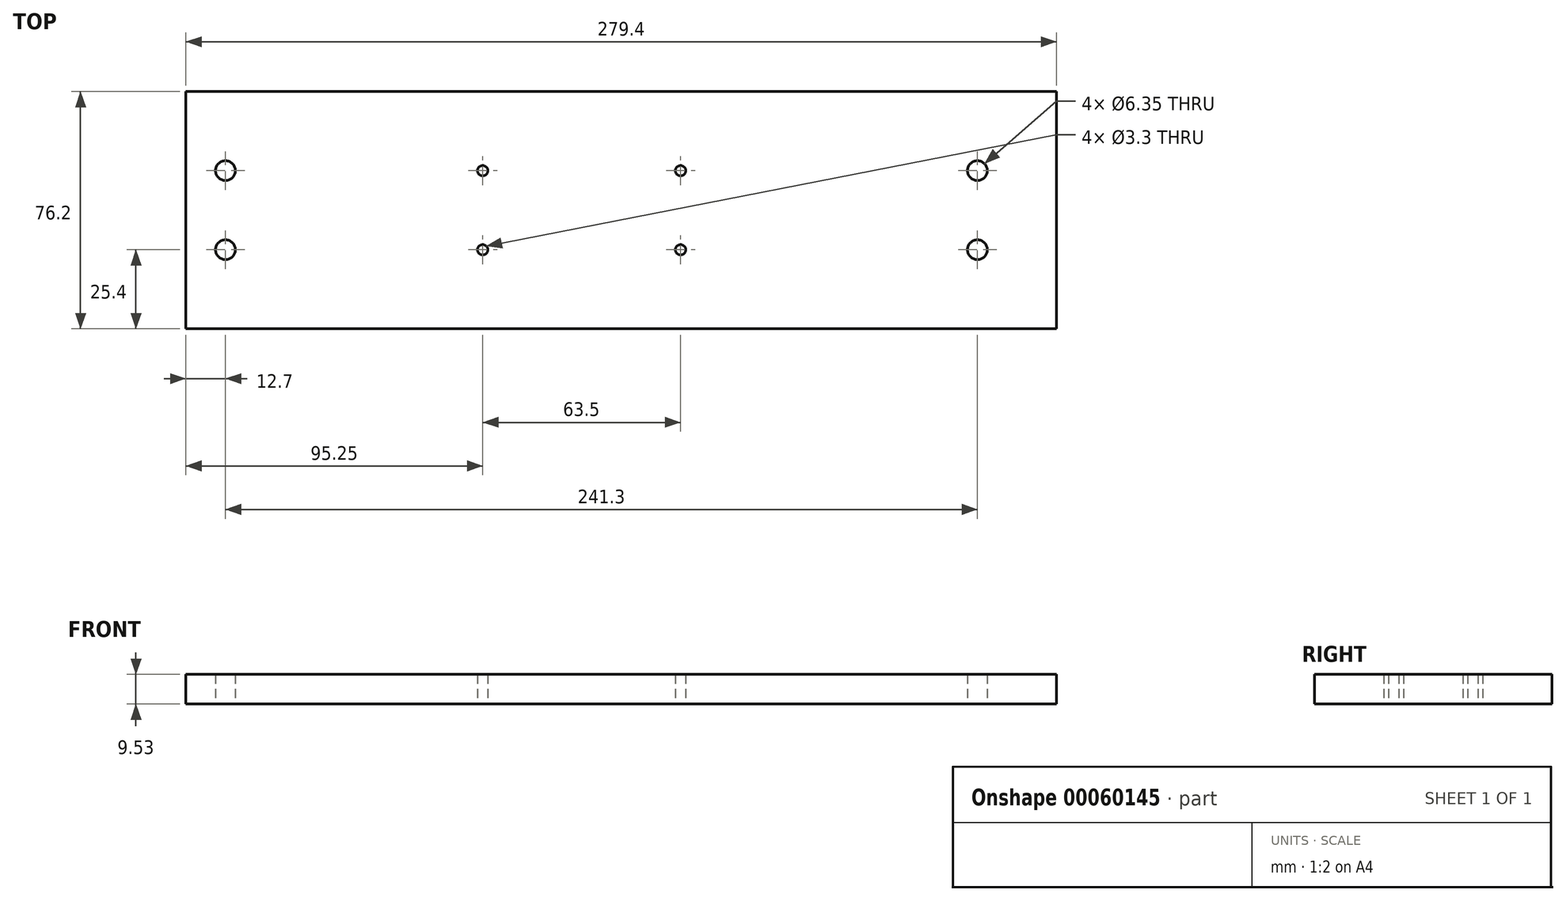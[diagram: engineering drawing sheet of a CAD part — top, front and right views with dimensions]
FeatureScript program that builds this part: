
annotation { "Feature Type Name" : "Feature", "Feature Type Description" : "" }
export const myFeature = defineFeature(function(context is Context, id is Id, definition is map)
    precondition{}
    {
        {
            var Q0;
            Q0=qCreatedBy(makeId("Top.planeOp"),FACE);
            var sketch = newSketch(context, id + "F0", { "sketchPlane" : qUnion([Q0])});
            skLineSegment(sketch, "E0.bottom", {"start": v(-152.4, 38.1) * mm, "end": v(127, 38.1) * mm});
            skLineSegment(sketch, "E0.top", {"start": v(-152.4, -38.1) * mm, "end": v(127, -38.1) * mm});
            skLineSegment(sketch, "E0.left", {"start": v(-152.4, 38.1) * mm, "end": v(-152.4, -38.1) * mm});
            skLineSegment(sketch, "E0.right", {"start": v(127, 38.1) * mm, "end": v(127, -38.1) * mm});
            skCircle(sketch, "E1", {"center": v(101.6, 12.7) * mm, "radius": 3.18 * mm});
            skCircle(sketch, "E2", {"center": v(6.35, 12.7) * mm, "radius": 1.65 * mm});
            skCircle(sketch, "E3", {"center": v(-57.15, 12.7) * mm, "radius": 1.65 * mm});
            skCircle(sketch, "E4", {"center": v(-139.7, 12.7) * mm, "radius": 3.18 * mm});
            skCircle(sketch, "E5", {"center": v(-139.7, -12.7) * mm, "radius": 3.18 * mm});
            skCircle(sketch, "E6", {"center": v(101.6, -12.7) * mm, "radius": 3.18 * mm});
            skCircle(sketch, "E7", {"center": v(6.35, -12.7) * mm, "radius": 1.65 * mm});
            skCircle(sketch, "E8", {"center": v(-57.15, -12.7) * mm, "radius": 1.65 * mm});
            skSolve(sketch);
        }
        {
            var Q0;
            Q0 = qSketchRegion(id + "F0", true);
            var Q1;
            Q1=makeQuery(id+"F0.imprint","IMPRINT",FACE,{"disambiguationData":[TD([[makeQuery(id+"F0.imprint","IMPRINT",EDGE,{"derivedFrom":sQuery(id+"F0.wireOp",EDGE,"E0.bottom")}),-1.0]])]});
            extrude(context, id + "F1", {"entities" : qUnion([Q0, Q1]), "depth" : 9.52 * mm});
        }
    });
